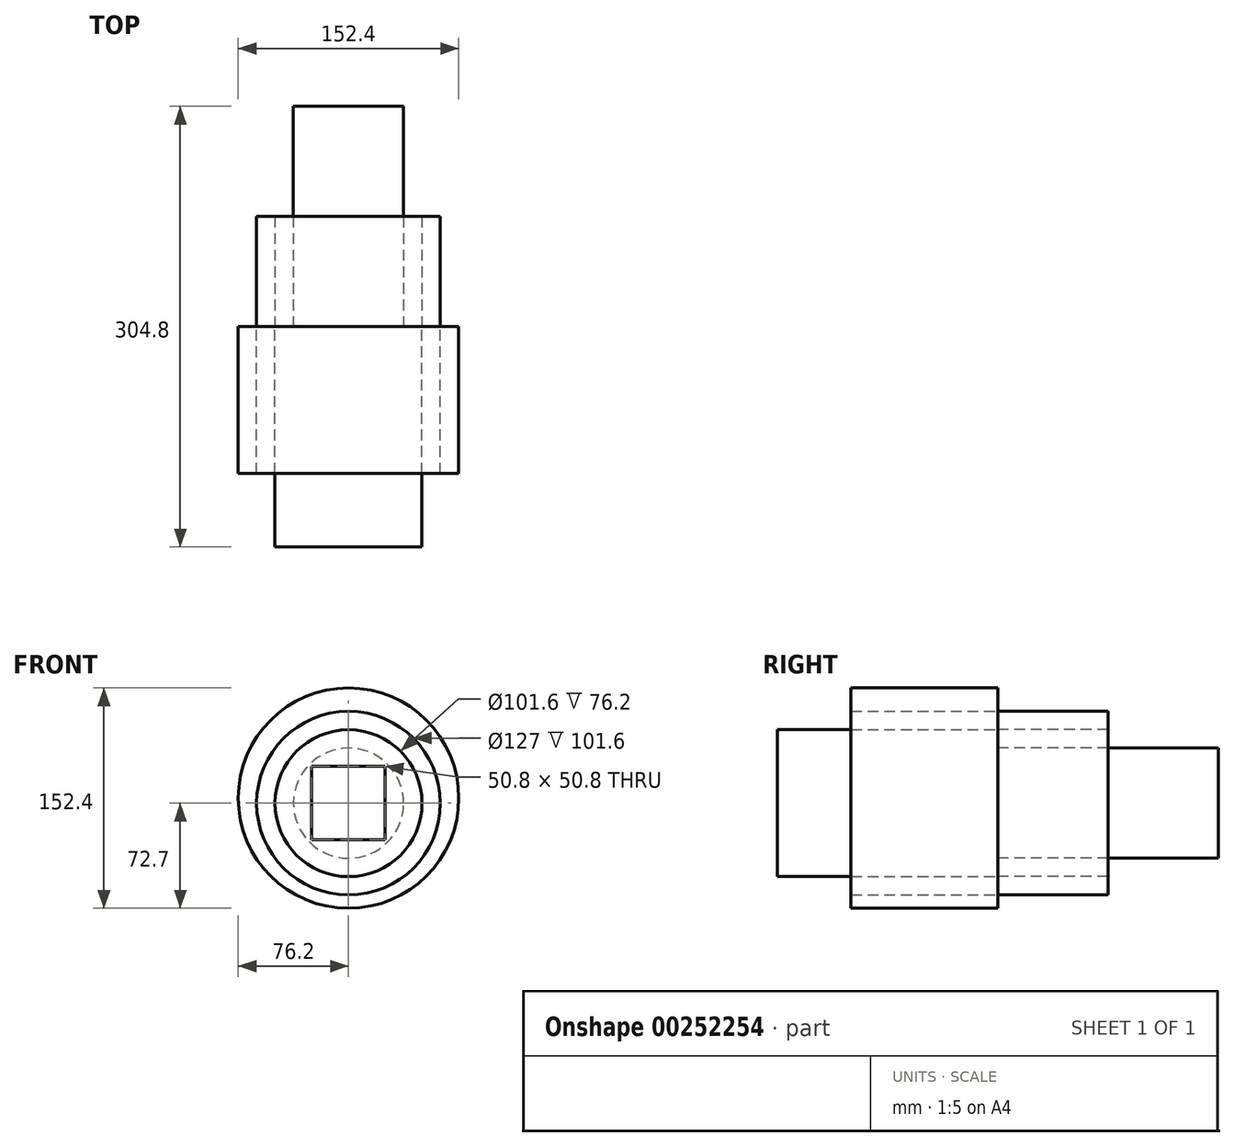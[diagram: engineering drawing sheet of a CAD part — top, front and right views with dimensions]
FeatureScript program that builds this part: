
annotation { "Feature Type Name" : "Feature", "Feature Type Description" : "" }
export const myFeature = defineFeature(function(context is Context, id is Id, definition is map)
    precondition{}
    {
        {
            var Q0;
            Q0=qCreatedBy(makeId("Front.planeOp"),FACE);
            var sketch = newSketch(context, id + "F0", { "sketchPlane" : qUnion([Q0])});
            skCircle(sketch, "E0", {"center": v(0, 3.5) * mm, "radius": 76.2 * mm});
            skCircle(sketch, "E1", {"center": v(0, 0) * mm, "radius": 63.5 * mm});
            skCircle(sketch, "E2", {"center": v(0, 0) * mm, "radius": 50.8 * mm});
            skCircle(sketch, "E3", {"center": v(0, 0) * mm, "radius": 38.1 * mm});
            skLineSegment(sketch, "E4.bottom", {"start": v(25.4, 25.4) * mm, "end": v(-25.4, 25.4) * mm});
            skLineSegment(sketch, "E4.top", {"start": v(25.4, -25.4) * mm, "end": v(-25.4, -25.4) * mm});
            skLineSegment(sketch, "E4.left", {"start": v(25.4, 25.4) * mm, "end": v(25.4, -25.4) * mm});
            skLineSegment(sketch, "E4.right", {"start": v(-25.4, 25.4) * mm, "end": v(-25.4, -25.4) * mm});
            skSolve(sketch);
        }
        {
            var Q0;
            Q0=makeQuery(id+"F0.imprint","IMPRINT",FACE,{"disambiguationData":[TD([[makeQuery(id+"F0.imprint","IMPRINT",EDGE,{"derivedFrom":sQuery(id+"F0.wireOp",EDGE,"E0")}),1.0]])]});
            extrude(context, id + "F1", {"entities" : qUnion([Q0]), "depth" : 101.6 * mm});
        }
        {
            var Q0;
            Q0=makeQuery(id+"F0.imprint","IMPRINT",FACE,{"disambiguationData":[TD([[makeQuery(id+"F0.imprint","IMPRINT",EDGE,{"derivedFrom":sQuery(id+"F0.wireOp",EDGE,"E1")}),1.0]])]});
            extrude(context, id + "F2", {"entities" : qUnion([Q0]), "operationType" : NewBodyOperationType.ADD, "oppositeDirection" : true, "depth" : 76.2 * mm});
        }
        {
            var Q0;
            Q0=makeQuery(id+"F0.imprint","IMPRINT",FACE,{"disambiguationData":[TD([[makeQuery(id+"F0.imprint","IMPRINT",EDGE,{"derivedFrom":sQuery(id+"F0.wireOp",EDGE,"E2")}),1.0]])]});
            extrude(context, id + "F3", {"entities" : qUnion([Q0]), "depth" : 152.4 * mm});
        }
        {
            var Q0;
            Q0=makeQuery(id+"F0.imprint","IMPRINT",FACE,{"disambiguationData":[TD([[makeQuery(id+"F0.imprint","IMPRINT",EDGE,{"derivedFrom":sQuery(id+"F0.wireOp",EDGE,"E3")}),1.0]])]});
            extrude(context, id + "F4", {"entities" : qUnion([Q0]), "operationType" : NewBodyOperationType.ADD, "endBound" : BoundingType.SYMMETRIC, "oppositeDirection" : true, "depth" : 304.8 * mm});
        }
    });
